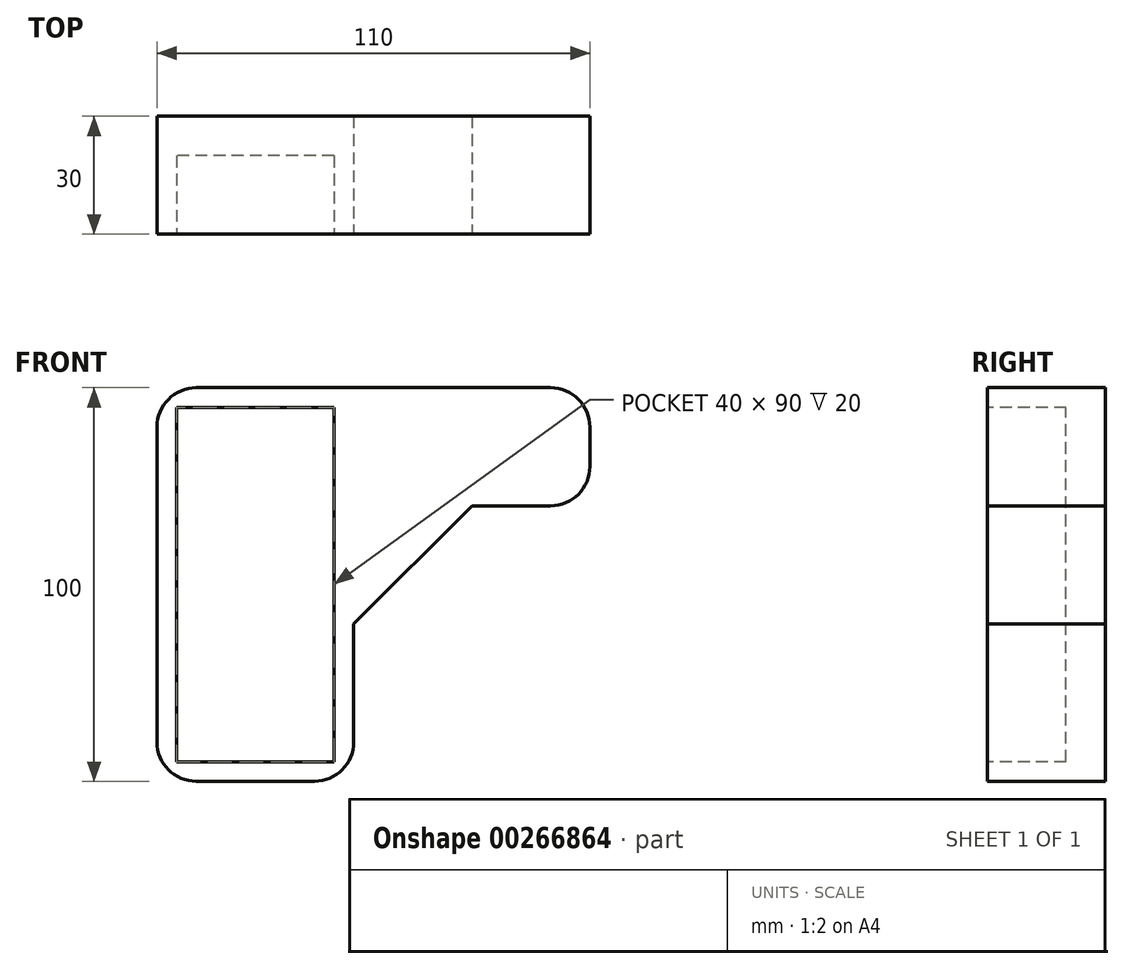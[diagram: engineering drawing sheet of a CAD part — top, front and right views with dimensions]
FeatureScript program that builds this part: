
annotation { "Feature Type Name" : "Feature", "Feature Type Description" : "" }
export const myFeature = defineFeature(function(context is Context, id is Id, definition is map)
    precondition{}
    {
        {
            var Q0;
            Q0=qCreatedBy(makeId("Front.planeOp"),FACE);
            var sketch = newSketch(context, id + "F0", { "sketchPlane" : qUnion([Q0])});
            skLineSegment(sketch, "E0", {"start": v(0, 0) * mm, "end": v(0, -30) * mm});
            skLineSegment(sketch, "E1", {"start": v(-10, -40) * mm, "end": v(-40, -40) * mm});
            skLineSegment(sketch, "E2", {"start": v(-50, -30) * mm, "end": v(-50, 50) * mm});
            skLineSegment(sketch, "E3", {"start": v(-40, 60) * mm, "end": v(50, 60) * mm});
            skLineSegment(sketch, "E4", {"start": v(60, 50) * mm, "end": v(60, 40) * mm});
            skLineSegment(sketch, "E5", {"start": v(50, 30) * mm, "end": v(30, 30) * mm});
            skLineSegment(sketch, "E6", {"start": v(0, 0) * mm, "end": v(30, 30) * mm});
            skPoint(sketch, "E7.visualSharp", {"position": v(-50, 60) * mm});
            skArc(sketch, "E7.filletArc", {"start": v(-40, 60) * mm, "mid": v(-47.07, 57.07) * mm, "end": v(-50, 50) * mm});
            skPoint(sketch, "E8.visualSharp", {"position": v(60, 60) * mm});
            skArc(sketch, "E8.filletArc", {"start": v(60, 50) * mm, "mid": v(57.07, 57.07) * mm, "end": v(50, 60) * mm});
            skPoint(sketch, "E9.visualSharp", {"position": v(60, 30) * mm});
            skArc(sketch, "E9.filletArc", {"start": v(50, 30) * mm, "mid": v(57.07, 32.93) * mm, "end": v(60, 40) * mm});
            skPoint(sketch, "E10.visualSharp", {"position": v(0, -40) * mm});
            skArc(sketch, "E10.filletArc", {"start": v(-10, -40) * mm, "mid": v(-2.93, -37.07) * mm, "end": v(0, -30) * mm});
            skPoint(sketch, "E11.visualSharp", {"position": v(-50, -40) * mm});
            skArc(sketch, "E11.filletArc", {"start": v(-50, -30) * mm, "mid": v(-47.07, -37.07) * mm, "end": v(-40, -40) * mm});
            skLineSegment(sketch, "E12", {"start": v(-45, 15) * mm, "end": v(-45, 55) * mm});
            skLineSegment(sketch, "E13", {"start": v(-45, 55) * mm, "end": v(-5, 55) * mm});
            skLineSegment(sketch, "E14", {"start": v(-5, 55) * mm, "end": v(-5, -35) * mm});
            skLineSegment(sketch, "E15", {"start": v(-5, -35) * mm, "end": v(-45, -35) * mm});
            skLineSegment(sketch, "E16", {"start": v(-45, -35) * mm, "end": v(-45, 15) * mm});
            skLineSegment(sketch, "E17", {"start": v(60, 45) * mm, "end": v(45, 45) * mm, "construction": true});
            skLineSegment(sketch, "E18", {"start": v(0, 0) * mm, "end": v(0, 30) * mm});
            skLineSegment(sketch, "E19", {"start": v(60, 30) * mm, "end": v(60, 9.21) * mm, "construction": true});
            skLineSegment(sketch, "E20", {"start": v(45, 60) * mm, "end": v(45, 9.21) * mm, "construction": true});
            skPoint(sketch, "E21", {"position": v(45, 45) * mm});
            skSolve(sketch);
        }
        {
            var Q0;
            Q0 = qSketchRegion(id + "F0", true);
            var Q1;
            Q1=makeQuery(id+"F0.imprint","IMPRINT",FACE,{"disambiguationData":[TD([[makeQuery(id+"F0.imprint","IMPRINT",EDGE,{"derivedFrom":sQuery(id+"F0.wireOp",EDGE,"E12")}),-1.0]])]});
            extrude(context, id + "F1", {"entities" : qUnion([Q0, Q1]), "oppositeDirection" : true, "depth" : 30 * mm});
        }
        {
            var Q0;
            Q0=makeQuery(id+"F0.imprint","IMPRINT",FACE,{"disambiguationData":[TD([[makeQuery(id+"F0.imprint","IMPRINT",EDGE,{"derivedFrom":sQuery(id+"F0.wireOp",EDGE,"E12")}),-1.0]])]});
            extrude(context, id + "F2", {"entities" : qUnion([Q0]), "operationType" : NewBodyOperationType.REMOVE, "oppositeDirection" : true, "depth" : 20 * mm});
        }
    });
